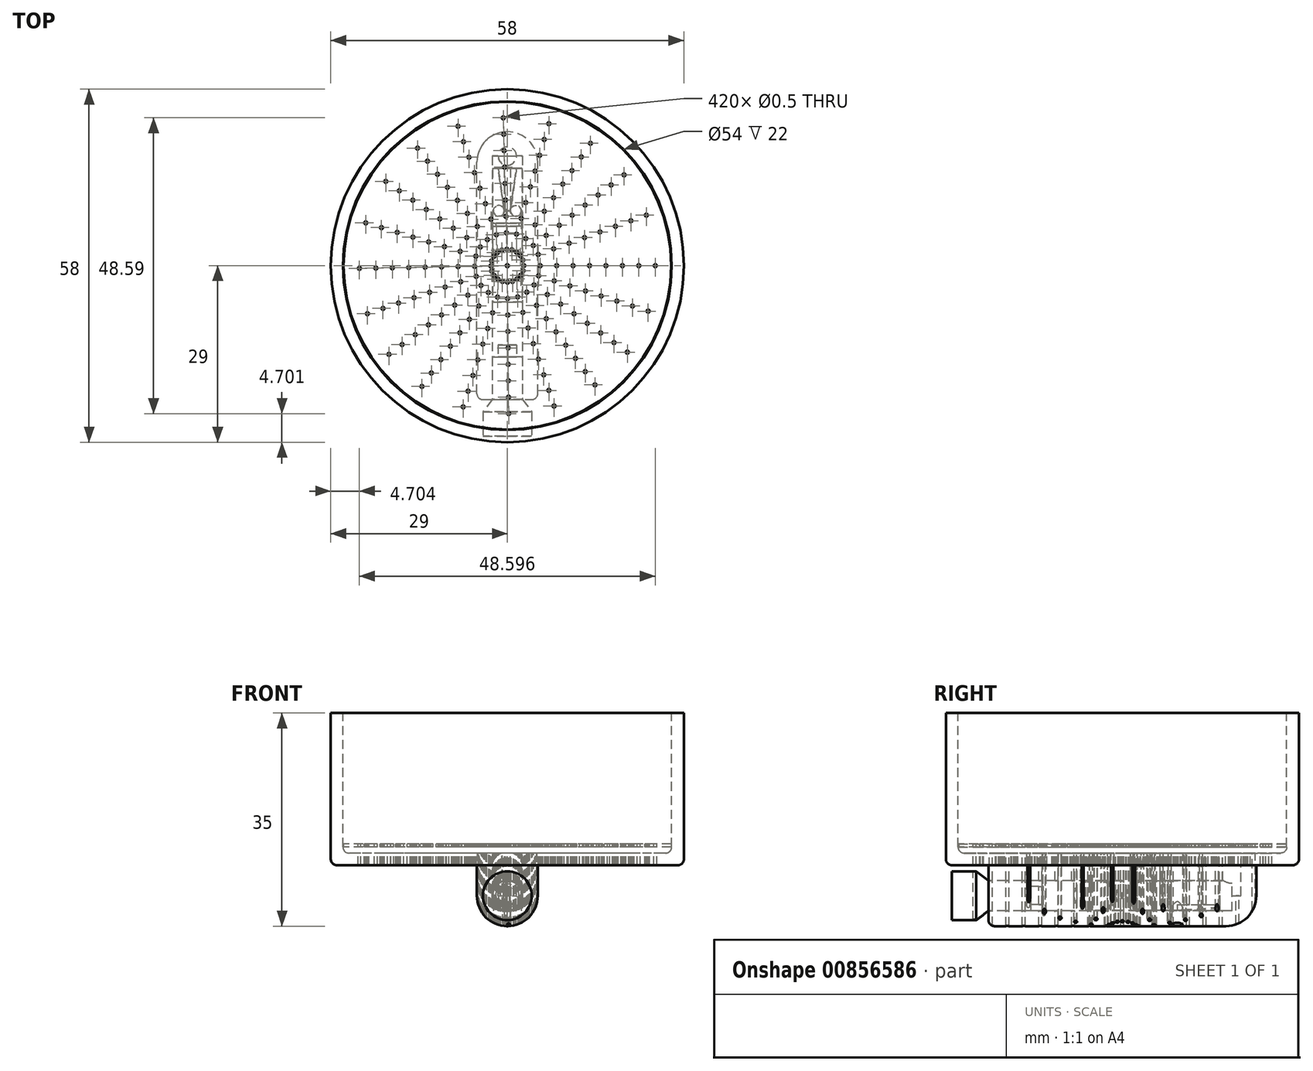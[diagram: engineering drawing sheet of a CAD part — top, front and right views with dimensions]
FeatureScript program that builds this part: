
annotation { "Feature Type Name" : "Feature", "Feature Type Description" : "" }
export const myFeature = defineFeature(function(context is Context, id is Id, definition is map)
    precondition{}
    {
        {
            var Q0;
            Q0=qCreatedBy(makeId("Top.planeOp"),FACE);
            var sketch = newSketch(context, id + "F0", { "sketchPlane" : qUnion([Q0])});
            skCircle(sketch, "E0", {"center": v(0, 0) * mm, "radius": 29 * mm});
            skSolve(sketch);
        }
        {
            var Q0;
            Q0=makeQuery(id+"F0.imprint","IMPRINT",FACE,{"disambiguationData":[TD([[makeQuery(id+"F0.imprint","IMPRINT",EDGE,{"derivedFrom":sQuery(id+"F0.wireOp",EDGE,"E0")}),1.0]])]});
            extrude(context, id + "F1", {"entities" : qUnion([Q0]), "oppositeDirection" : true, "depth" : 25 * mm, "offsetDistance" : 25 * mm});
        }
        {
            var Q0;
            Q0=makeQuery(id+"F1.opExtrude","CAP_FACE",FACE,{"disambiguationData":[OSD([sQuery(id+"F0.wireOp",EDGE,"E0")])],"isStart":true});
            shell(context, id + "F2", {"entities" : qUnion([Q0]), "thickness" : 2 * mm});
        }
        {
            var Q0;
            Q0=qCreatedBy(makeId("Front.planeOp"),FACE);
            var sketch = newSketch(context, id + "F3", { "sketchPlane" : qUnion([Q0])});
            skLineSegment(sketch, "E1.bottom", {"start": v(-5, -25) * mm, "end": v(5, -25) * mm});
            skLineSegment(sketch, "E1.top", {"start": v(-5, -35) * mm, "end": v(5, -35) * mm});
            skLineSegment(sketch, "E1.left", {"start": v(-5, -25) * mm, "end": v(-5, -35) * mm});
            skLineSegment(sketch, "E1.right", {"start": v(5, -25) * mm, "end": v(5, -35) * mm});
            skLineSegment(sketch, "E2.0", {"start": v(-29, -25) * mm, "end": v(29, -25) * mm});
            skSolve(sketch);
        }
        {
            var Q0;
            Q0=makeQuery(id+"F3.imprint","IMPRINT",FACE,{"disambiguationData":[TD([[makeQuery(id+"F3.imprint","IMPRINT",EDGE,{"derivedFrom":sQuery(id+"F3.wireOp",EDGE,"E1.top")}),1.0]])]});
            extrude(context, id + "F4", {"entities" : qUnion([Q0]), "operationType" : NewBodyOperationType.ADD, "depth" : 22 * mm, "offsetDistance" : 25 * mm, "hasSecondDirection" : true, "secondDirectionOppositeDirection" : true, "secondDirectionDepth" : 22 * mm});
        }
        {
            var Q0;
            Q0=makeQuery(id+"F4.opExtrude","CAP_FACE",FACE,{"disambiguationData":[OSD([sQuery(id+"F3.wireOp",EDGE,"E1.top"),sQuery(id+"F3.wireOp",EDGE,"E1.left"),sQuery(id+"F3.wireOp",EDGE,"E1.right"),sQuery(id+"F3.wireOp",EDGE,"E2.0")])],"isStart":false});
            var sketch = newSketch(context, id + "F5", { "sketchPlane" : qUnion([Q0])});
            skCircle(sketch, "E3", {"center": v(0, -30) * mm, "radius": 2.5 * mm});
            skLineSegment(sketch, "E4", {"start": v(-7.7, -30) * mm, "end": v(7.12, -30) * mm, "construction": true});
            skPoint(sketch, "E5", {"position": v(0, -32.45) * mm});
            skSolve(sketch);
        }
        {
            var Q0;
            Q0=makeQuery(id+"F5.imprint","IMPRINT",FACE,{"disambiguationData":[TD([[makeQuery(id+"F5.imprint","IMPRINT",EDGE,{"derivedFrom":sQuery(id+"F5.wireOp",EDGE,"E3")}),1.0]])]});
            extrude(context, id + "F6", {"entities" : qUnion([Q0]), "operationType" : NewBodyOperationType.REMOVE, "oppositeDirection" : true, "depth" : 40 * mm, "offsetDistance" : 25 * mm});
        }
        {
            var Q0;
            Q0=makeQuery(id+"F5.imprint","IMPRINT",FACE,{"disambiguationData":[TD([[makeQuery(id+"F5.imprint","IMPRINT",EDGE,{"derivedFrom":sQuery(id+"F5.wireOp",EDGE,"E3")}),-1.0]])]});
            cPlane(context, id + "F7", {"entities" : qUnion([Q0]), "cplaneType" : CPlaneType.OFFSET, "offset" : 20 * mm, "oppositeDirection" : true, "width" : 150 * mm, "height" : 150 * mm});
        }
        {
            var Q0;
            Q0=qCreatedBy(id+"F7.planeOp",FACE);
            var sketch = newSketch(context, id + "F8", { "sketchPlane" : qUnion([Q0])});
            skCircle(sketch, "E6", {"center": v(0, -30) * mm, "radius": 2.43 * mm});
            skSolve(sketch);
        }
        {
            var Q0;
            Q0=makeQuery(id+"F8.imprint","IMPRINT",FACE,{"disambiguationData":[TD([[makeQuery(id+"F8.imprint","IMPRINT",EDGE,{"derivedFrom":sQuery(id+"F8.wireOp",EDGE,"E6")}),1.0]])]});
            extrude(context, id + "F9", {"entities" : qUnion([Q0]), "oppositeDirection" : true, "depth" : 18 * mm, "offsetDistance" : 25 * mm, "hasSecondDirection" : true, "secondDirectionOppositeDirection" : false, "secondDirectionDepth" : 4 * mm});
        }
        {
            var Q0;
            Q0=sQuery(id+"F5.wireOp",VERTEX,"E5");
            var Q1;
            Q1=qCreatedBy(makeId("Top.planeOp"),FACE);
            cPlane(context, id + "F10", {"entities" : qUnion([Q0, Q1]), "cplaneType" : CPlaneType.PLANE_POINT, "offset" : 25 * mm, "width" : 150 * mm, "height" : 150 * mm});
        }
        {
            var Q0;
            Q0=qCreatedBy(id+"F10.planeOp",FACE);
            var sketch = newSketch(context, id + "F11", { "sketchPlane" : qUnion([Q0])});
            skLineSegment(sketch, "E7", {"start": v(-0.5, 9) * mm, "end": v(0.5, 9) * mm});
            skLineSegment(sketch, "E8", {"start": v(0.5, 9) * mm, "end": v(1.5, 16) * mm});
            skLineSegment(sketch, "E9", {"start": v(-0.5, 9) * mm, "end": v(-1.5, 16) * mm});
            skLineSegment(sketch, "E10", {"start": v(-1.5, 16) * mm, "end": v(1.5, 16) * mm});
            skLineSegment(sketch, "E11", {"start": v(0, -13.78) * mm, "end": v(0, 12.24) * mm, "construction": true});
            skLineSegment(sketch, "E12.0", {"start": v(2.43, 16) * mm, "end": v(-2.43, 16) * mm, "construction": true});
            skSolve(sketch);
        }
        {
            var Q0;
            Q0=makeQuery(id+"F11.imprint","IMPRINT",FACE,{"disambiguationData":[TD([[makeQuery(id+"F11.imprint","IMPRINT",EDGE,{"derivedFrom":sQuery(id+"F11.wireOp",EDGE,"E8")}),1.0]])]});
            extrude(context, id + "F12", {"entities" : qUnion([Q0]), "operationType" : NewBodyOperationType.REMOVE, "depth" : 1 * mm, "offsetDistance" : 25 * mm});
        }
        {
            var Q0;
            Q0=sQuery(id+"F5.wireOp",VERTEX,"E3.center");
            var Q1;
            Q1=qCreatedBy(makeId("Top.planeOp"),FACE);
            cPlane(context, id + "F13", {"entities" : qUnion([Q0, Q1]), "cplaneType" : CPlaneType.PLANE_POINT, "offset" : 25 * mm, "width" : 150 * mm, "height" : 150 * mm});
        }
        {
            var Q0;
            Q0=qCreatedBy(id+"F13.planeOp",FACE);
            var sketch = newSketch(context, id + "F14", { "sketchPlane" : qUnion([Q0])});
            skLineSegment(sketch, "E13.0", {"start": v(2.43, -6) * mm, "end": v(-2.43, -6) * mm, "construction": true});
            skLineSegment(sketch, "E14.bottom", {"start": v(1.92, 6.5) * mm, "end": v(2.42, 6.5) * mm});
            skLineSegment(sketch, "E14.top", {"start": v(1.92, 7) * mm, "end": v(2.42, 7) * mm});
            skLineSegment(sketch, "E14.left", {"start": v(1.92, 6.5) * mm, "end": v(1.92, 7) * mm});
            skLineSegment(sketch, "E14.right", {"start": v(2.42, 6.5) * mm, "end": v(2.42, 7) * mm});
            skLineSegment(sketch, "E15", {"start": v(0, 0) * mm, "end": v(0, -5.82) * mm, "construction": true});
            skPoint(sketch, "E15.endSnap0", {"position": v(0, -6) * mm});
            skSolve(sketch);
        }
        {
            var Q0;
            Q0=makeQuery(id+"F14.imprint","IMPRINT",FACE,{"disambiguationData":[TD([[makeQuery(id+"F14.imprint","IMPRINT",EDGE,{"derivedFrom":sQuery(id+"F14.wireOp",EDGE,"E14.bottom")}),1.0]])]});
            var Q1;
            Q1=sQuery(id+"F14.wireOp",EDGE,"E15");
            revolve(context, id + "F15", {"operationType" : NewBodyOperationType.REMOVE, "surfaceOperationType" : NewSurfaceOperationType.NEW, "entities" : qUnion([Q0]), "axis" : qUnion([Q1]), "revolveType" : RevolveType.FULL, "oppositeDirection" : true});
        }
        {
            var Q0;
            Q0=makeQuery(id+"F4.opExtrude","SWEPT_FACE",FACE,{"disambiguationData":[OSD([sQuery(id+"F3.wireOp",EDGE,"E1.top")])]});
            var sketch = newSketch(context, id + "F16", { "sketchPlane" : qUnion([Q0])});
            skCircle(sketch, "E16", {"center": v(1.4, -9) * mm, "radius": 0.9 * mm});
            skCircle(sketch, "E17", {"center": v(-1.4, -9) * mm, "radius": 0.9 * mm});
            skSolve(sketch);
        }
        {
            var Q0;
            Q0=makeQuery(id+"F16.imprint","IMPRINT",FACE,{"disambiguationData":[TD([[makeQuery(id+"F16.imprint","IMPRINT",EDGE,{"derivedFrom":sQuery(id+"F16.wireOp",EDGE,"E17")}),1.0]])]});
            var Q1;
            Q1=makeQuery(id+"F16.imprint","IMPRINT",FACE,{"disambiguationData":[TD([[makeQuery(id+"F16.imprint","IMPRINT",EDGE,{"derivedFrom":sQuery(id+"F16.wireOp",EDGE,"E16")}),1.0]])]});
            var Q2;
            Q2=makeQuery(id+"F9.opExtrude","SWEPT_BODY",BODY,{"disambiguationData":[OSD([sQuery(id+"F8.wireOp",EDGE,"E6")])]});
            extrude(context, id + "F17", {"entities" : qUnion([Q0, Q1]), "operationType" : NewBodyOperationType.REMOVE, "endBound" : BoundingType.UP_TO_NEXT, "oppositeDirection" : true, "depth" : 25 * mm, "endBoundEntityBody" : qUnion([Q2]), "offsetDistance" : 25 * mm});
        }
        {
            var Q0;
            {var subQ0=sQuery(id+"F0.wireOp",EDGE,"E0");Q0=makeQuery(id+"F2.opShell","OFFSET_FACE",FACE,{"disambiguationData":[OSD([subQ0]),TDD([makeQuery(id+"F1.opExtrude","CAP_FACE",FACE,{"disambiguationData":[OSD([subQ0])],"isStart":false})])]});}
            var sketch = newSketch(context, id + "F18", { "sketchPlane" : qUnion([Q0])});
            skCircle(sketch, "E18", {"center": v(0, 18) * mm, "radius": 1.5 * mm});
            skCircle(sketch, "E19.0.0", {"center": v(0, 0) * mm, "radius": 29 * mm});
            skPoint(sketch, "E20.0", {"position": v(0, 16) * mm});
            skPoint(sketch, "E21", {"position": v(0, 19.5) * mm});
            skSolve(sketch);
        }
        {
            var Q0;
            Q0=makeQuery(id+"F18.imprint","IMPRINT",FACE,{"disambiguationData":[TD([[makeQuery(id+"F18.imprint","IMPRINT",EDGE,{"derivedFrom":sQuery(id+"F18.wireOp",EDGE,"E18")}),1.0]])]});
            var Q1;
            Q1=sQuery(id+"F5.wireOp",VERTEX,"E3.center");
            extrude(context, id + "F19", {"entities" : qUnion([Q0]), "operationType" : NewBodyOperationType.REMOVE, "endBound" : BoundingType.UP_TO_VERTEX, "oppositeDirection" : true, "depth" : 25 * mm, "endBoundEntityVertex" : qUnion([Q1]), "offsetDistance" : 25 * mm});
        }
        {
            var Q0;
            Q0=qCreatedBy(id+"F13.planeOp",FACE);
            var sketch = newSketch(context, id + "F20", { "sketchPlane" : qUnion([Q0])});
            skLineSegment(sketch, "E22.0", {"start": v(2.5, -22) * mm, "end": v(-2.5, -22) * mm, "construction": true});
            skLineSegment(sketch, "E23", {"start": v(2.5, -22) * mm, "end": v(4, -24) * mm});
            skLineSegment(sketch, "E24", {"start": v(0, -27) * mm, "end": v(0, -13) * mm});
            skPoint(sketch, "E24.endSnap0", {"position": v(0, -22) * mm});
            skLineSegment(sketch, "E25", {"start": v(0, -13) * mm, "end": v(1.5, -13) * mm});
            skLineSegment(sketch, "E26", {"start": v(1.5, -13) * mm, "end": v(1.5, -15) * mm});
            skLineSegment(sketch, "E27", {"start": v(1.5, -15) * mm, "end": v(2.5, -15) * mm});
            skLineSegment(sketch, "E28", {"start": v(2.5, -15) * mm, "end": v(2.5, -22) * mm});
            skLineSegment(sketch, "E29", {"start": v(0, -27) * mm, "end": v(0, -28) * mm});
            skLineSegment(sketch, "E30", {"start": v(0, -28) * mm, "end": v(4, -28) * mm});
            skLineSegment(sketch, "E31", {"start": v(4, -28) * mm, "end": v(4, -24) * mm});
            skSolve(sketch);
        }
        {
            var Q0;
            Q0=makeQuery(id+"F20.imprint","IMPRINT",FACE,{"disambiguationData":[TD([[makeQuery(id+"F20.imprint","IMPRINT",EDGE,{"derivedFrom":sQuery(id+"F20.wireOp",EDGE,"E23")}),-1.0]])]});
            var Q1;
            Q1=sQuery(id+"F20.wireOp",EDGE,"E24");
            revolve(context, id + "F21", {"surfaceOperationType" : NewSurfaceOperationType.NEW, "entities" : qUnion([Q0]), "axis" : qUnion([Q1]), "revolveType" : RevolveType.FULL});
        }
        {
            var Q0;
            {var subQ0=sQuery(id+"F0.wireOp",EDGE,"E0");Q0=makeQuery(id+"F2.opShell","OFFSET_FACE",FACE,{"disambiguationData":[OSD([subQ0]),TDD([makeQuery(id+"F1.opExtrude","CAP_FACE",FACE,{"disambiguationData":[OSD([subQ0])],"isStart":false})])]});}
            cPlane(context, id + "F22", {"entities" : qUnion([Q0]), "cplaneType" : CPlaneType.OFFSET, "offset" : 1 * mm, "width" : 150 * mm, "height" : 150 * mm});
        }
        {
            var Q0;
            Q0=qCreatedBy(id+"F22.planeOp",FACE);
            var sketch = newSketch(context, id + "F23", { "sketchPlane" : qUnion([Q0])});
            skCircle(sketch, "E32", {"center": v(0, 0) * mm, "radius": 26.9 * mm});
            skSolve(sketch);
        }
        {
            var Q0;
            Q0=makeQuery(id+"F23.imprint","IMPRINT",FACE,{"disambiguationData":[TD([[makeQuery(id+"F23.imprint","IMPRINT",EDGE,{"derivedFrom":sQuery(id+"F23.wireOp",EDGE,"E32")}),1.0]])]});
            extrude(context, id + "F24", {"entities" : qUnion([Q0]), "depth" : 0.5 * mm, "offsetDistance" : 25 * mm});
        }
        {
            var Q0;
            Q0=makeQuery(id+"F24.opExtrude","CAP_FACE",FACE,{"disambiguationData":[OSD([sQuery(id+"F23.wireOp",EDGE,"E32")])],"isStart":false});
            var sketch = newSketch(context, id + "F25", { "sketchPlane" : qUnion([Q0])});
            skCircle(sketch, "E33", {"center": v(0, 0) * mm, "radius": 0.25 * mm});
            skCircle(sketch, "E34.1.0.0", {"center": v(2.7, 0) * mm, "radius": 0.25 * mm});
            skCircle(sketch, "E34.2.0.0", {"center": v(5.4, 0) * mm, "radius": 0.25 * mm});
            skCircle(sketch, "E34.3.0.0", {"center": v(8.1, 0) * mm, "radius": 0.25 * mm});
            skCircle(sketch, "E34.4.0.0", {"center": v(10.8, 0) * mm, "radius": 0.25 * mm});
            skCircle(sketch, "E34.5.0.0", {"center": v(13.5, 0) * mm, "radius": 0.25 * mm});
            skCircle(sketch, "E34.6.0.0", {"center": v(16.2, 0) * mm, "radius": 0.25 * mm});
            skCircle(sketch, "E34.7.0.0", {"center": v(18.9, 0) * mm, "radius": 0.25 * mm});
            skCircle(sketch, "E34.8.0.0", {"center": v(21.6, 0) * mm, "radius": 0.25 * mm});
            skCircle(sketch, "E34.9.0.0", {"center": v(24.3, 0) * mm, "radius": 0.25 * mm});
            skLineSegment(sketch, "E34.direction1", {"start": v(0, 0) * mm, "end": v(2.7, 0) * mm, "construction": true});
            skLineSegment(sketch, "E35.1.0", {"start": v(0, 0) * mm, "end": v(2.57, -0.83) * mm, "construction": true});
            skCircle(sketch, "E35.1.1", {"center": v(15.42, -4.98) * mm, "radius": 0.25 * mm});
            skCircle(sketch, "E35.1.2", {"center": v(10.28, -3.32) * mm, "radius": 0.25 * mm});
            skCircle(sketch, "E35.1.3", {"center": v(12.85, -4.15) * mm, "radius": 0.25 * mm});
            skCircle(sketch, "E35.1.4", {"center": v(7.7, -2.49) * mm, "radius": 0.25 * mm});
            skCircle(sketch, "E35.1.5", {"center": v(23.12, -7.47) * mm, "radius": 0.25 * mm});
            skCircle(sketch, "E35.1.6", {"center": v(20.56, -6.64) * mm, "radius": 0.25 * mm});
            skCircle(sketch, "E35.1.7", {"center": v(17.99, -5.8) * mm, "radius": 0.25 * mm});
            skCircle(sketch, "E35.1.8", {"center": v(5.14, -1.66) * mm, "radius": 0.25 * mm});
            skCircle(sketch, "E35.1.9", {"center": v(2.57, -0.83) * mm, "radius": 0.25 * mm});
            skLineSegment(sketch, "E35.2.0", {"start": v(0, 0) * mm, "end": v(2.2, -1.58) * mm, "construction": true});
            skCircle(sketch, "E35.2.1", {"center": v(13.14, -9.47) * mm, "radius": 0.25 * mm});
            skCircle(sketch, "E35.2.2", {"center": v(8.76, -6.32) * mm, "radius": 0.25 * mm});
            skCircle(sketch, "E35.2.3", {"center": v(10.95, -7.9) * mm, "radius": 0.25 * mm});
            skCircle(sketch, "E35.2.4", {"center": v(6.57, -4.74) * mm, "radius": 0.25 * mm});
            skCircle(sketch, "E35.2.5", {"center": v(19.71, -14.21) * mm, "radius": 0.25 * mm});
            skCircle(sketch, "E35.2.6", {"center": v(17.52, -12.63) * mm, "radius": 0.25 * mm});
            skCircle(sketch, "E35.2.7", {"center": v(15.33, -11.05) * mm, "radius": 0.25 * mm});
            skCircle(sketch, "E35.2.8", {"center": v(4.38, -3.16) * mm, "radius": 0.25 * mm});
            skCircle(sketch, "E35.2.9", {"center": v(2.2, -1.58) * mm, "radius": 0.25 * mm});
            skLineSegment(sketch, "E35.3.0", {"start": v(0, 0) * mm, "end": v(1.6, -2.18) * mm, "construction": true});
            skCircle(sketch, "E35.3.1", {"center": v(9.6, -13.05) * mm, "radius": 0.25 * mm});
            skCircle(sketch, "E35.3.2", {"center": v(6.4, -8.7) * mm, "radius": 0.25 * mm});
            skCircle(sketch, "E35.3.3", {"center": v(8, -10.88) * mm, "radius": 0.25 * mm});
            skCircle(sketch, "E35.3.4", {"center": v(4.8, -6.53) * mm, "radius": 0.25 * mm});
            skCircle(sketch, "E35.3.5", {"center": v(14.4, -19.58) * mm, "radius": 0.25 * mm});
            skCircle(sketch, "E35.3.6", {"center": v(12.8, -17.4) * mm, "radius": 0.25 * mm});
            skCircle(sketch, "E35.3.7", {"center": v(11.2, -15.23) * mm, "radius": 0.25 * mm});
            skCircle(sketch, "E35.3.8", {"center": v(3.2, -4.35) * mm, "radius": 0.25 * mm});
            skCircle(sketch, "E35.3.9", {"center": v(1.6, -2.18) * mm, "radius": 0.25 * mm});
            skLineSegment(sketch, "E35.4.0", {"start": v(0, 0) * mm, "end": v(0.85, -2.56) * mm, "construction": true});
            skCircle(sketch, "E35.4.1", {"center": v(5.12, -15.37) * mm, "radius": 0.25 * mm});
            skCircle(sketch, "E35.4.2", {"center": v(3.41, -10.25) * mm, "radius": 0.25 * mm});
            skCircle(sketch, "E35.4.3", {"center": v(4.27, -12.8) * mm, "radius": 0.25 * mm});
            skCircle(sketch, "E35.4.4", {"center": v(2.56, -7.68) * mm, "radius": 0.25 * mm});
            skCircle(sketch, "E35.4.5", {"center": v(7.68, -23.05) * mm, "radius": 0.25 * mm});
            skCircle(sketch, "E35.4.6", {"center": v(6.83, -20.5) * mm, "radius": 0.25 * mm});
            skCircle(sketch, "E35.4.7", {"center": v(5.97, -17.93) * mm, "radius": 0.25 * mm});
            skCircle(sketch, "E35.4.8", {"center": v(1.7, -5.12) * mm, "radius": 0.25 * mm});
            skCircle(sketch, "E35.4.9", {"center": v(0.85, -2.56) * mm, "radius": 0.25 * mm});
            skLineSegment(sketch, "E35.5.0", {"start": v(0, 0) * mm, "end": v(0.02, -2.7) * mm, "construction": true});
            skCircle(sketch, "E35.5.1", {"center": v(0.15, -16.2) * mm, "radius": 0.25 * mm});
            skCircle(sketch, "E35.5.2", {"center": v(0.1, -10.8) * mm, "radius": 0.25 * mm});
            skCircle(sketch, "E35.5.3", {"center": v(0.12, -13.5) * mm, "radius": 0.25 * mm});
            skCircle(sketch, "E35.5.4", {"center": v(0.07, -8.1) * mm, "radius": 0.25 * mm});
            skCircle(sketch, "E35.5.5", {"center": v(0.22, -24.3) * mm, "radius": 0.25 * mm});
            skCircle(sketch, "E35.5.6", {"center": v(0.2, -21.6) * mm, "radius": 0.25 * mm});
            skCircle(sketch, "E35.5.7", {"center": v(0.17, -18.9) * mm, "radius": 0.25 * mm});
            skCircle(sketch, "E35.5.8", {"center": v(0.05, -5.4) * mm, "radius": 0.25 * mm});
            skCircle(sketch, "E35.5.9", {"center": v(0.02, -2.7) * mm, "radius": 0.25 * mm});
            skLineSegment(sketch, "E35.6.0", {"start": v(0, 0) * mm, "end": v(-0.8, -2.58) * mm, "construction": true});
            skCircle(sketch, "E35.6.1", {"center": v(-4.84, -15.46) * mm, "radius": 0.25 * mm});
            skCircle(sketch, "E35.6.2", {"center": v(-3.22, -10.3) * mm, "radius": 0.25 * mm});
            skCircle(sketch, "E35.6.3", {"center": v(-4.03, -12.88) * mm, "radius": 0.25 * mm});
            skCircle(sketch, "E35.6.4", {"center": v(-2.42, -7.73) * mm, "radius": 0.25 * mm});
            skCircle(sketch, "E35.6.5", {"center": v(-7.25, -23.2) * mm, "radius": 0.25 * mm});
            skCircle(sketch, "E35.6.6", {"center": v(-6.45, -20.62) * mm, "radius": 0.25 * mm});
            skCircle(sketch, "E35.6.7", {"center": v(-5.64, -18.04) * mm, "radius": 0.25 * mm});
            skCircle(sketch, "E35.6.8", {"center": v(-1.61, -5.15) * mm, "radius": 0.25 * mm});
            skCircle(sketch, "E35.6.9", {"center": v(-0.8, -2.58) * mm, "radius": 0.25 * mm});
            skLineSegment(sketch, "E35.7.0", {"start": v(0, 0) * mm, "end": v(-1.56, -2.2) * mm, "construction": true});
            skCircle(sketch, "E35.7.1", {"center": v(-9.35, -13.23) * mm, "radius": 0.25 * mm});
            skCircle(sketch, "E35.7.2", {"center": v(-6.24, -8.82) * mm, "radius": 0.25 * mm});
            skCircle(sketch, "E35.7.3", {"center": v(-7.8, -11.02) * mm, "radius": 0.25 * mm});
            skCircle(sketch, "E35.7.4", {"center": v(-4.68, -6.61) * mm, "radius": 0.25 * mm});
            skCircle(sketch, "E35.7.5", {"center": v(-14.03, -19.84) * mm, "radius": 0.25 * mm});
            skCircle(sketch, "E35.7.6", {"center": v(-12.47, -17.64) * mm, "radius": 0.25 * mm});
            skCircle(sketch, "E35.7.7", {"center": v(-10.91, -15.43) * mm, "radius": 0.25 * mm});
            skCircle(sketch, "E35.7.8", {"center": v(-3.12, -4.4) * mm, "radius": 0.25 * mm});
            skCircle(sketch, "E35.7.9", {"center": v(-1.56, -2.2) * mm, "radius": 0.25 * mm});
            skLineSegment(sketch, "E35.8.0", {"start": v(0, 0) * mm, "end": v(-2.16, -1.62) * mm, "construction": true});
            skCircle(sketch, "E35.8.1", {"center": v(-12.96, -9.71) * mm, "radius": 0.25 * mm});
            skCircle(sketch, "E35.8.2", {"center": v(-8.64, -6.48) * mm, "radius": 0.25 * mm});
            skCircle(sketch, "E35.8.3", {"center": v(-10.8, -8.1) * mm, "radius": 0.25 * mm});
            skCircle(sketch, "E35.8.4", {"center": v(-6.48, -4.86) * mm, "radius": 0.25 * mm});
            skCircle(sketch, "E35.8.5", {"center": v(-19.45, -14.57) * mm, "radius": 0.25 * mm});
            skCircle(sketch, "E35.8.6", {"center": v(-17.29, -12.95) * mm, "radius": 0.25 * mm});
            skCircle(sketch, "E35.8.7", {"center": v(-15.13, -11.33) * mm, "radius": 0.25 * mm});
            skCircle(sketch, "E35.8.8", {"center": v(-4.32, -3.24) * mm, "radius": 0.25 * mm});
            skCircle(sketch, "E35.8.9", {"center": v(-2.16, -1.62) * mm, "radius": 0.25 * mm});
            skLineSegment(sketch, "E35.9.0", {"start": v(0, 0) * mm, "end": v(-2.55, -0.88) * mm, "construction": true});
            skCircle(sketch, "E35.9.1", {"center": v(-15.32, -5.26) * mm, "radius": 0.25 * mm});
            skCircle(sketch, "E35.9.2", {"center": v(-10.21, -3.5) * mm, "radius": 0.25 * mm});
            skCircle(sketch, "E35.9.3", {"center": v(-12.77, -4.38) * mm, "radius": 0.25 * mm});
            skCircle(sketch, "E35.9.4", {"center": v(-7.66, -2.63) * mm, "radius": 0.25 * mm});
            skCircle(sketch, "E35.9.5", {"center": v(-22.98, -7.9) * mm, "radius": 0.25 * mm});
            skCircle(sketch, "E35.9.6", {"center": v(-20.43, -7.01) * mm, "radius": 0.25 * mm});
            skCircle(sketch, "E35.9.7", {"center": v(-17.88, -6.14) * mm, "radius": 0.25 * mm});
            skCircle(sketch, "E35.9.8", {"center": v(-5.1, -1.75) * mm, "radius": 0.25 * mm});
            skCircle(sketch, "E35.9.9", {"center": v(-2.55, -0.88) * mm, "radius": 0.25 * mm});
            skLineSegment(sketch, "E35.10.0", {"start": v(0, 0) * mm, "end": v(-2.7, -0.05) * mm, "construction": true});
            skCircle(sketch, "E35.10.1", {"center": v(-16.2, -0.3) * mm, "radius": 0.25 * mm});
            skCircle(sketch, "E35.10.2", {"center": v(-10.8, -0.2) * mm, "radius": 0.25 * mm});
            skCircle(sketch, "E35.10.3", {"center": v(-13.5, -0.25) * mm, "radius": 0.25 * mm});
            skCircle(sketch, "E35.10.4", {"center": v(-8.1, -0.15) * mm, "radius": 0.25 * mm});
            skCircle(sketch, "E35.10.5", {"center": v(-24.3, -0.45) * mm, "radius": 0.25 * mm});
            skCircle(sketch, "E35.10.6", {"center": v(-21.6, -0.4) * mm, "radius": 0.25 * mm});
            skCircle(sketch, "E35.10.7", {"center": v(-18.9, -0.35) * mm, "radius": 0.25 * mm});
            skCircle(sketch, "E35.10.8", {"center": v(-5.4, -0.1) * mm, "radius": 0.25 * mm});
            skCircle(sketch, "E35.10.9", {"center": v(-2.7, -0.05) * mm, "radius": 0.25 * mm});
            skLineSegment(sketch, "E35.11.0", {"start": v(0, 0) * mm, "end": v(-2.58, 0.78) * mm, "construction": true});
            skCircle(sketch, "E35.11.1", {"center": v(-15.5, 4.7) * mm, "radius": 0.25 * mm});
            skCircle(sketch, "E35.11.2", {"center": v(-10.34, 3.13) * mm, "radius": 0.25 * mm});
            skCircle(sketch, "E35.11.3", {"center": v(-12.92, 3.91) * mm, "radius": 0.25 * mm});
            skCircle(sketch, "E35.11.4", {"center": v(-7.75, 2.35) * mm, "radius": 0.25 * mm});
            skCircle(sketch, "E35.11.5", {"center": v(-23.26, 7.04) * mm, "radius": 0.25 * mm});
            skCircle(sketch, "E35.11.6", {"center": v(-20.67, 6.26) * mm, "radius": 0.25 * mm});
            skCircle(sketch, "E35.11.7", {"center": v(-18.09, 5.48) * mm, "radius": 0.25 * mm});
            skCircle(sketch, "E35.11.8", {"center": v(-5.17, 1.56) * mm, "radius": 0.25 * mm});
            skCircle(sketch, "E35.11.9", {"center": v(-2.58, 0.78) * mm, "radius": 0.25 * mm});
            skLineSegment(sketch, "E35.12.0", {"start": v(0, 0) * mm, "end": v(-2.22, 1.54) * mm, "construction": true});
            skCircle(sketch, "E35.12.1", {"center": v(-13.31, 9.23) * mm, "radius": 0.25 * mm});
            skCircle(sketch, "E35.12.2", {"center": v(-8.88, 6.15) * mm, "radius": 0.25 * mm});
            skCircle(sketch, "E35.12.3", {"center": v(-11.1, 7.7) * mm, "radius": 0.25 * mm});
            skCircle(sketch, "E35.12.4", {"center": v(-6.66, 4.62) * mm, "radius": 0.25 * mm});
            skCircle(sketch, "E35.12.5", {"center": v(-19.97, 13.85) * mm, "radius": 0.25 * mm});
            skCircle(sketch, "E35.12.6", {"center": v(-17.75, 12.3) * mm, "radius": 0.25 * mm});
            skCircle(sketch, "E35.12.7", {"center": v(-15.53, 10.77) * mm, "radius": 0.25 * mm});
            skCircle(sketch, "E35.12.8", {"center": v(-4.44, 3.08) * mm, "radius": 0.25 * mm});
            skCircle(sketch, "E35.12.9", {"center": v(-2.22, 1.54) * mm, "radius": 0.25 * mm});
            skLineSegment(sketch, "E35.13.0", {"start": v(0, 0) * mm, "end": v(-1.64, 2.15) * mm, "construction": true});
            skCircle(sketch, "E35.13.1", {"center": v(-9.83, 12.87) * mm, "radius": 0.25 * mm});
            skCircle(sketch, "E35.13.2", {"center": v(-6.55, 8.58) * mm, "radius": 0.25 * mm});
            skCircle(sketch, "E35.13.3", {"center": v(-8.2, 10.73) * mm, "radius": 0.25 * mm});
            skCircle(sketch, "E35.13.4", {"center": v(-4.92, 6.44) * mm, "radius": 0.25 * mm});
            skCircle(sketch, "E35.13.5", {"center": v(-14.75, 19.31) * mm, "radius": 0.25 * mm});
            skCircle(sketch, "E35.13.6", {"center": v(-13.1, 17.17) * mm, "radius": 0.25 * mm});
            skCircle(sketch, "E35.13.7", {"center": v(-11.47, 15.02) * mm, "radius": 0.25 * mm});
            skCircle(sketch, "E35.13.8", {"center": v(-3.28, 4.3) * mm, "radius": 0.25 * mm});
            skCircle(sketch, "E35.13.9", {"center": v(-1.64, 2.15) * mm, "radius": 0.25 * mm});
            skLineSegment(sketch, "E35.14.0", {"start": v(0, 0) * mm, "end": v(-0.9, 2.55) * mm, "construction": true});
            skCircle(sketch, "E35.14.1", {"center": v(-5.4, 15.27) * mm, "radius": 0.25 * mm});
            skCircle(sketch, "E35.14.2", {"center": v(-3.6, 10.18) * mm, "radius": 0.25 * mm});
            skCircle(sketch, "E35.14.3", {"center": v(-4.5, 12.73) * mm, "radius": 0.25 * mm});
            skCircle(sketch, "E35.14.4", {"center": v(-2.7, 7.64) * mm, "radius": 0.25 * mm});
            skCircle(sketch, "E35.14.5", {"center": v(-8.1, 22.9) * mm, "radius": 0.25 * mm});
            skCircle(sketch, "E35.14.6", {"center": v(-7.2, 20.36) * mm, "radius": 0.25 * mm});
            skCircle(sketch, "E35.14.7", {"center": v(-6.3, 17.82) * mm, "radius": 0.25 * mm});
            skCircle(sketch, "E35.14.8", {"center": v(-1.8, 5.1) * mm, "radius": 0.25 * mm});
            skCircle(sketch, "E35.14.9", {"center": v(-0.9, 2.55) * mm, "radius": 0.25 * mm});
            skLineSegment(sketch, "E35.15.0", {"start": v(0, 0) * mm, "end": v(-0.07, 2.7) * mm, "construction": true});
            skCircle(sketch, "E35.15.1", {"center": v(-0.45, 16.2) * mm, "radius": 0.25 * mm});
            skCircle(sketch, "E35.15.2", {"center": v(-0.3, 10.8) * mm, "radius": 0.25 * mm});
            skCircle(sketch, "E35.15.3", {"center": v(-0.37, 13.5) * mm, "radius": 0.25 * mm});
            skCircle(sketch, "E35.15.4", {"center": v(-0.22, 8.1) * mm, "radius": 0.25 * mm});
            skCircle(sketch, "E35.15.5", {"center": v(-0.67, 24.3) * mm, "radius": 0.25 * mm});
            skCircle(sketch, "E35.15.6", {"center": v(-0.6, 21.6) * mm, "radius": 0.25 * mm});
            skCircle(sketch, "E35.15.7", {"center": v(-0.52, 18.9) * mm, "radius": 0.25 * mm});
            skCircle(sketch, "E35.15.8", {"center": v(-0.15, 5.4) * mm, "radius": 0.25 * mm});
            skCircle(sketch, "E35.15.9", {"center": v(-0.07, 2.7) * mm, "radius": 0.25 * mm});
            skLineSegment(sketch, "E35.16.0", {"start": v(0, 0) * mm, "end": v(0.76, 2.6) * mm, "construction": true});
            skCircle(sketch, "E35.16.1", {"center": v(4.55, 15.55) * mm, "radius": 0.25 * mm});
            skCircle(sketch, "E35.16.2", {"center": v(3.03, 10.37) * mm, "radius": 0.25 * mm});
            skCircle(sketch, "E35.16.3", {"center": v(3.8, 12.96) * mm, "radius": 0.25 * mm});
            skCircle(sketch, "E35.16.4", {"center": v(2.28, 7.77) * mm, "radius": 0.25 * mm});
            skCircle(sketch, "E35.16.5", {"center": v(6.83, 23.32) * mm, "radius": 0.25 * mm});
            skCircle(sketch, "E35.16.6", {"center": v(6.07, 20.73) * mm, "radius": 0.25 * mm});
            skCircle(sketch, "E35.16.7", {"center": v(5.3, 18.14) * mm, "radius": 0.25 * mm});
            skCircle(sketch, "E35.16.8", {"center": v(1.52, 5.18) * mm, "radius": 0.25 * mm});
            skCircle(sketch, "E35.16.9", {"center": v(0.76, 2.6) * mm, "radius": 0.25 * mm});
            skLineSegment(sketch, "E35.17.0", {"start": v(0, 0) * mm, "end": v(1.52, 2.23) * mm, "construction": true});
            skCircle(sketch, "E35.17.1", {"center": v(9.1, 13.4) * mm, "radius": 0.25 * mm});
            skCircle(sketch, "E35.17.2", {"center": v(6.07, 8.93) * mm, "radius": 0.25 * mm});
            skCircle(sketch, "E35.17.3", {"center": v(7.6, 11.16) * mm, "radius": 0.25 * mm});
            skCircle(sketch, "E35.17.4", {"center": v(4.55, 6.7) * mm, "radius": 0.25 * mm});
            skCircle(sketch, "E35.17.5", {"center": v(13.66, 20.1) * mm, "radius": 0.25 * mm});
            skCircle(sketch, "E35.17.6", {"center": v(12.14, 17.86) * mm, "radius": 0.25 * mm});
            skCircle(sketch, "E35.17.7", {"center": v(10.63, 15.63) * mm, "radius": 0.25 * mm});
            skCircle(sketch, "E35.17.8", {"center": v(3.04, 4.47) * mm, "radius": 0.25 * mm});
            skCircle(sketch, "E35.17.9", {"center": v(1.52, 2.23) * mm, "radius": 0.25 * mm});
            skLineSegment(sketch, "E35.18.0", {"start": v(0, 0) * mm, "end": v(2.13, 1.66) * mm, "construction": true});
            skCircle(sketch, "E35.18.1", {"center": v(12.78, 9.95) * mm, "radius": 0.25 * mm});
            skCircle(sketch, "E35.18.2", {"center": v(8.52, 6.63) * mm, "radius": 0.25 * mm});
            skCircle(sketch, "E35.18.3", {"center": v(10.65, 8.3) * mm, "radius": 0.25 * mm});
            skCircle(sketch, "E35.18.4", {"center": v(6.4, 4.98) * mm, "radius": 0.25 * mm});
            skCircle(sketch, "E35.18.5", {"center": v(19.18, 14.93) * mm, "radius": 0.25 * mm});
            skCircle(sketch, "E35.18.6", {"center": v(17.05, 13.27) * mm, "radius": 0.25 * mm});
            skCircle(sketch, "E35.18.7", {"center": v(14.91, 11.6) * mm, "radius": 0.25 * mm});
            skCircle(sketch, "E35.18.8", {"center": v(4.26, 3.32) * mm, "radius": 0.25 * mm});
            skCircle(sketch, "E35.18.9", {"center": v(2.13, 1.66) * mm, "radius": 0.25 * mm});
            skLineSegment(sketch, "E35.19.0", {"start": v(0, 0) * mm, "end": v(2.54, 0.92) * mm, "construction": true});
            skCircle(sketch, "E35.19.1", {"center": v(15.22, 5.54) * mm, "radius": 0.25 * mm});
            skCircle(sketch, "E35.19.2", {"center": v(10.15, 3.7) * mm, "radius": 0.25 * mm});
            skCircle(sketch, "E35.19.3", {"center": v(12.69, 4.62) * mm, "radius": 0.25 * mm});
            skCircle(sketch, "E35.19.4", {"center": v(7.61, 2.77) * mm, "radius": 0.25 * mm});
            skCircle(sketch, "E35.19.5", {"center": v(22.83, 8.31) * mm, "radius": 0.25 * mm});
            skCircle(sketch, "E35.19.6", {"center": v(20.3, 7.39) * mm, "radius": 0.25 * mm});
            skCircle(sketch, "E35.19.7", {"center": v(17.76, 6.46) * mm, "radius": 0.25 * mm});
            skCircle(sketch, "E35.19.8", {"center": v(5.07, 1.85) * mm, "radius": 0.25 * mm});
            skCircle(sketch, "E35.19.9", {"center": v(2.54, 0.92) * mm, "radius": 0.25 * mm});
            skLineSegment(sketch, "E35.anchor2", {"start": v(0, 0) * mm, "end": v(2.54, 0.92) * mm, "construction": true});
            skSolve(sketch);
        }
        {
            var Q0;
            Q0 = qSketchRegion(id + "F25", true);
            extrude(context, id + "F26", {"entities" : qUnion([Q0]), "operationType" : NewBodyOperationType.REMOVE, "endBound" : BoundingType.THROUGH_ALL, "oppositeDirection" : true, "depth" : 25 * mm, "offsetDistance" : 25 * mm});
        }
        {
            var Q0;
            {var subQ0=sQuery(id+"F0.wireOp",EDGE,"E0");Q0=makeQuery(id+"F2.opShell","OFFSET_EDGE",EDGE,{"disambiguationData":[OSD([subQ0]),TDD([makeQuery(id+"F1.opExtrude","CAP_EDGE",EDGE,{"disambiguationData":[OSD([subQ0])],"isStart":false})])]});}
            fillet(context, id + "F27", {"entities" : qUnion([Q0]), "radius" : 1 * mm, "tangentPropagation" : true, "allowEdgeOverflow" : false});
        }
        {
            var Q0;
            Q0=makeQuery(id+"F4.opExtrude","SWEPT_EDGE",EDGE,{"disambiguationData":[OSD([sQuery(id+"F3.wireOp",EDGE,"E1.right"),sQuery(id+"F3.wireOp",EDGE,"E2.0")])]});
            var Q1;
            Q1=makeQuery(id+"F4.opExtrude","SWEPT_EDGE",EDGE,{"disambiguationData":[OSD([sQuery(id+"F3.wireOp",EDGE,"E1.top"),sQuery(id+"F3.wireOp",EDGE,"E1.right")])]});
            var Q2;
            Q2=makeQuery(id+"F4.opExtrude","SWEPT_EDGE",EDGE,{"disambiguationData":[OSD([sQuery(id+"F3.wireOp",EDGE,"E1.top"),sQuery(id+"F3.wireOp",EDGE,"E1.left")])]});
            var Q3;
            Q3=makeQuery(id+"F4.opExtrude","SWEPT_EDGE",EDGE,{"disambiguationData":[OSD([sQuery(id+"F3.wireOp",EDGE,"E1.left"),sQuery(id+"F3.wireOp",EDGE,"E2.0")])]});
            fillet(context, id + "F28", {"entities" : qUnion([Q0, Q1, Q2, Q3]), "radius" : 5 * mm, "tangentPropagation" : true, "allowEdgeOverflow" : false});
        }
        {
            var Q0;
            {var subQ0=sQuery(id+"F3.wireOp",EDGE,"E1.left");var subQ1=sQuery(id+"F3.wireOp",EDGE,"E1.top");Q0=makeQuery(id+"F28.opFillet","BLEND_EDGE",EDGE,{"blendedFrom":[makeQuery(id+"F4.opExtrude","SWEPT_EDGE",EDGE,{"disambiguationData":[OSD([subQ1,subQ0])]}),makeQuery(id+"F4.opExtrude","CAP_FACE",FACE,{"disambiguationData":[OSD([subQ1,subQ0,sQuery(id+"F3.wireOp",EDGE,"E1.right"),sQuery(id+"F3.wireOp",EDGE,"E2.0")])],"isStart":true})],"blendedInto":[makeQuery(id+"F4.opExtrude","CAP_FACE",FACE,{"disambiguationData":[OSD([subQ1,subQ0,sQuery(id+"F3.wireOp",EDGE,"E1.right"),sQuery(id+"F3.wireOp",EDGE,"E2.0")])],"isStart":true})]});}
            fillet(context, id + "F29", {"entities" : qUnion([Q0]), "radius" : 5 * mm, "tangentPropagation" : true, "allowEdgeOverflow" : false});
        }
        {
            var Q0;
            {var subQ0=sQuery(id+"F3.wireOp",EDGE,"E1.left");var subQ1=sQuery(id+"F3.wireOp",EDGE,"E1.top");Q0=makeQuery(id+"F28.opFillet","BLEND_EDGE",EDGE,{"blendedFrom":[makeQuery(id+"F4.opExtrude","SWEPT_EDGE",EDGE,{"disambiguationData":[OSD([subQ1,subQ0])]}),makeQuery(id+"F4.opExtrude","CAP_FACE",FACE,{"disambiguationData":[OSD([subQ1,subQ0,sQuery(id+"F3.wireOp",EDGE,"E1.right"),sQuery(id+"F3.wireOp",EDGE,"E2.0")])],"isStart":false})],"blendedInto":[makeQuery(id+"F4.opExtrude","CAP_FACE",FACE,{"disambiguationData":[OSD([subQ1,subQ0,sQuery(id+"F3.wireOp",EDGE,"E1.right"),sQuery(id+"F3.wireOp",EDGE,"E2.0")])],"isStart":false})]});}
            fillet(context, id + "F30", {"entities" : qUnion([Q0]), "radius" : 1 * mm, "tangentPropagation" : true, "allowEdgeOverflow" : false});
        }
        {
            var Q0;
            Q0=makeQuery(id+"F1.opExtrude","CAP_EDGE",EDGE,{"disambiguationData":[OSD([sQuery(id+"F0.wireOp",EDGE,"E0")])],"isStart":false});
            fillet(context, id + "F31", {"entities" : qUnion([Q0]), "radius" : 1 * mm, "tangentPropagation" : true, "allowEdgeOverflow" : false});
        }
    });
